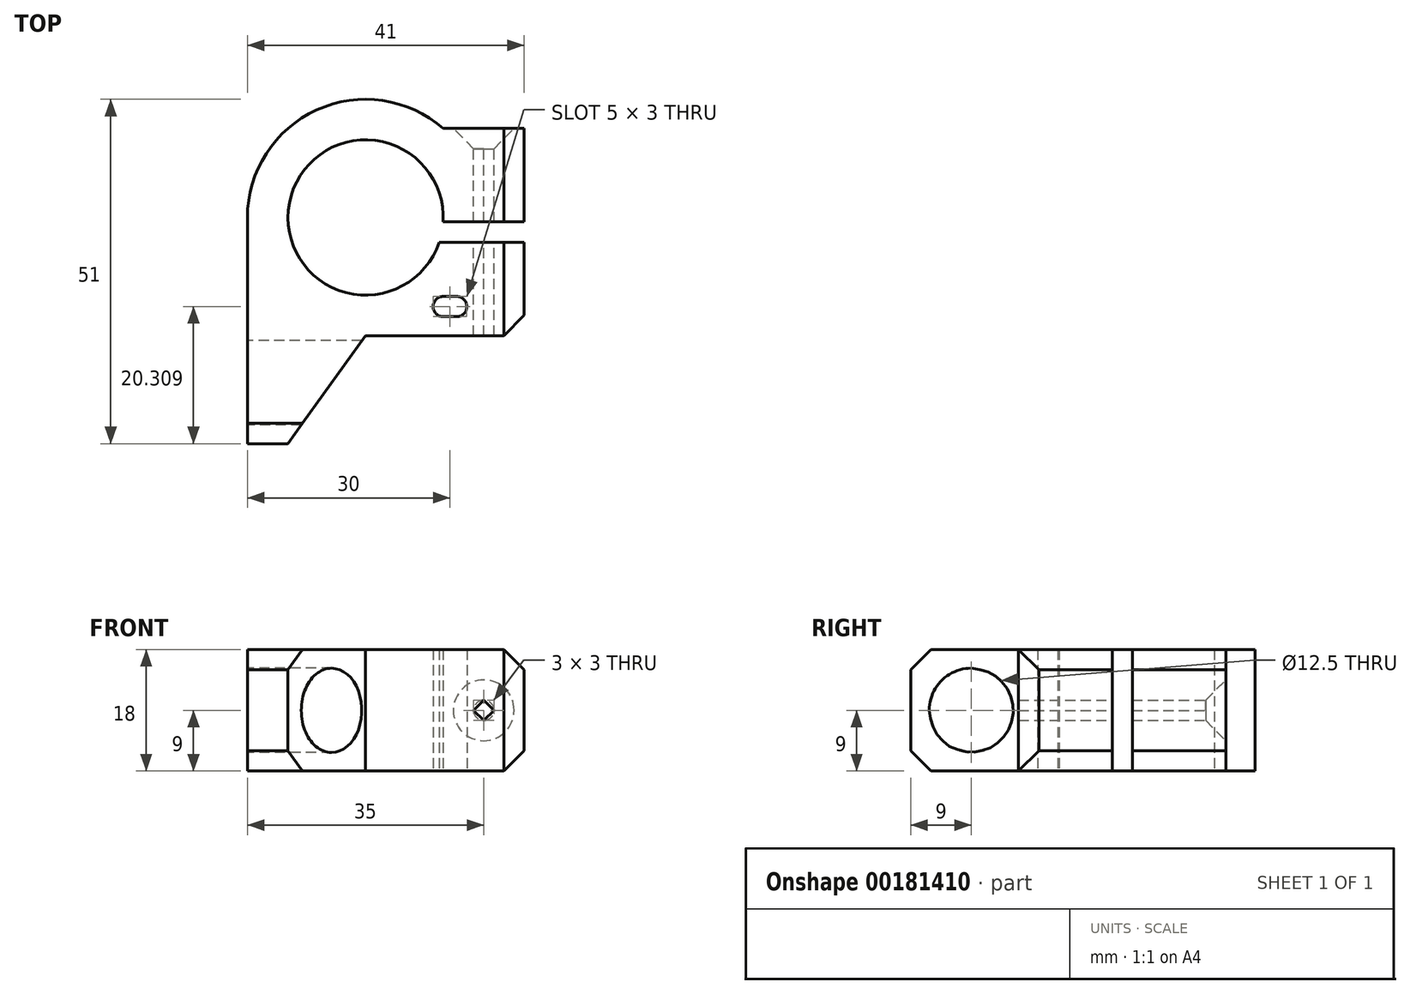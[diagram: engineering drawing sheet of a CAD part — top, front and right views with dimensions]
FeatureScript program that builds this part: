
annotation { "Feature Type Name" : "Feature", "Feature Type Description" : "" }
export const myFeature = defineFeature(function(context is Context, id is Id, definition is map)
    precondition{}
    {
        {
            var Q0;
            Q0=qCreatedBy(makeId("Top.planeOp"),FACE);
            var sketch = newSketch(context, id + "F0", { "sketchPlane" : qUnion([Q0])});
            skCircle(sketch, "E0", {"center": v(0, 0) * mm, "radius": 11.5 * mm});
            skArc(sketch, "E1", {"start": v(0, -17.5) * mm, "mid": v(6.14, -16.39) * mm, "end": v(11.5, -13.2) * mm, "construction": true});
            skLineSegment(sketch, "E2.bottom", {"start": v(-17.5, 0) * mm, "end": v(-11.5, 0) * mm, "construction": true});
            skLineSegment(sketch, "E2.top", {"start": v(-17.5, -33.5) * mm, "end": v(-11.5, -33.5) * mm});
            skLineSegment(sketch, "E2.left", {"start": v(-17.5, 0) * mm, "end": v(-17.5, -33.5) * mm});
            skLineSegment(sketch, "E3", {"start": v(0, -17.5) * mm, "end": v(-17.5, -17.5) * mm, "construction": true});
            skLineSegment(sketch, "E4", {"start": v(-11.5, -33.5) * mm, "end": v(0, -17.5) * mm});
            skLineSegment(sketch, "E5.bottom", {"start": v(11.5, 13.2) * mm, "end": v(23.5, 13.2) * mm});
            skLineSegment(sketch, "E5.top", {"start": v(11.5, -13.2) * mm, "end": v(23.5, -13.2) * mm, "construction": true});
            skLineSegment(sketch, "E5.left", {"start": v(11.5, 13.2) * mm, "end": v(11.5, 0) * mm, "construction": true});
            skLineSegment(sketch, "E5.right", {"start": v(23.5, 13.2) * mm, "end": v(23.5, -13.2) * mm});
            skPoint(sketch, "E5.middle", {"position": v(17.5, 0) * mm});
            skArc(sketch, "E6.trimOffspring", {"start": v(11.5, 13.2) * mm, "mid": v(-7.25, 15.93) * mm, "end": v(-17.5, 0) * mm});
            skLineSegment(sketch, "E7", {"start": v(0, -17.5) * mm, "end": v(23.5, -17.5) * mm});
            skLineSegment(sketch, "E8", {"start": v(23.5, -17.5) * mm, "end": v(23.5, -13.2) * mm});
            skLineSegment(sketch, "E9", {"start": v(11.5, -13.2) * mm, "end": v(13.5, -13.2) * mm});
            skArc(sketch, "E10.0.startCap", {"start": v(11.5, -14.7) * mm, "mid": v(10, -13.2) * mm, "end": v(11.5, -11.7) * mm});
            skArc(sketch, "E10.0.endCap", {"start": v(13.5, -11.7) * mm, "mid": v(15, -13.2) * mm, "end": v(13.5, -14.7) * mm});
            skLineSegment(sketch, "E10.0.left", {"start": v(11.5, -11.7) * mm, "end": v(13.5, -11.7) * mm});
            skLineSegment(sketch, "E10.0.right", {"start": v(11.5, -14.7) * mm, "end": v(13.5, -14.7) * mm});
            skSolve(sketch);
        }
        {
            var Q0;
            Q0=makeQuery(id+"F0.imprint","IMPRINT",FACE,{"disambiguationData":[TD([[makeQuery(id+"F0.imprint","IMPRINT",EDGE,{"derivedFrom":sQuery(id+"F0.wireOp",EDGE,"E0")}),-1.0]])]});
            extrude(context, id + "F1", {"entities" : qUnion([Q0]), "depth" : 18 * mm});
        }
        {
            var Q0;
            Q0=makeQuery(id+"F1.opExtrude","SWEPT_FACE",FACE,{"disambiguationData":[OSD([sQuery(id+"F0.wireOp",EDGE,"E2.left")])]});
            var sketch = newSketch(context, id + "F2", { "sketchPlane" : qUnion([Q0])});
            skCircle(sketch, "E11", {"center": v(24.5, 9) * mm, "radius": 6.25 * mm});
            skLineSegment(sketch, "E12", {"start": v(33.5, 9) * mm, "end": v(24.5, 9) * mm, "construction": true});
            skSolve(sketch);
        }
        {
            var Q0;
            Q0=makeQuery(id+"F2.imprint","IMPRINT",FACE,{"disambiguationData":[TD([[makeQuery(id+"F2.imprint","IMPRINT",EDGE,{"derivedFrom":sQuery(id+"F2.wireOp",EDGE,"E11")}),1.0]])]});
            extrude(context, id + "F3", {"entities" : qUnion([Q0]), "operationType" : NewBodyOperationType.REMOVE, "endBound" : BoundingType.THROUGH_ALL, "oppositeDirection" : true, "depth" : 25 * mm});
        }
        {
            var Q0;
            Q0=makeQuery(id+"F1.opExtrude","SWEPT_FACE",FACE,{"disambiguationData":[OSD([sQuery(id+"F0.wireOp",EDGE,"E5.bottom")])]});
            var sketch = newSketch(context, id + "F4", { "sketchPlane" : qUnion([Q0])});
            skLineSegment(sketch, "E13", {"start": v(-17.5, 18) * mm, "end": v(-17.5, 0) * mm, "construction": true});
            skLineSegment(sketch, "E14", {"start": v(-11.5, 9) * mm, "end": v(-23.5, 9) * mm, "construction": true});
            skCircle(sketch, "E15", {"center": v(-17.5, 9) * mm, "radius": 4.5 * mm});
            skLineSegment(sketch, "E16.bottom", {"start": v(-19, 7.5) * mm, "end": v(-16, 7.5) * mm, "construction": true});
            skLineSegment(sketch, "E16.top", {"start": v(-19, 10.5) * mm, "end": v(-16, 10.5) * mm, "construction": true});
            skLineSegment(sketch, "E16.left", {"start": v(-19, 7.5) * mm, "end": v(-19, 10.5) * mm, "construction": true});
            skLineSegment(sketch, "E16.right", {"start": v(-16, 7.5) * mm, "end": v(-16, 10.5) * mm, "construction": true});
            skLineSegment(sketch, "E17", {"start": v(-17.5, 10.5) * mm, "end": v(-19, 9) * mm});
            skLineSegment(sketch, "E18", {"start": v(-19, 9) * mm, "end": v(-17.5, 7.5) * mm});
            skLineSegment(sketch, "E19", {"start": v(-17.5, 7.5) * mm, "end": v(-16, 9) * mm});
            skLineSegment(sketch, "E20", {"start": v(-16, 9) * mm, "end": v(-17.5, 10.5) * mm});
            skSolve(sketch);
        }
        {
            var Q0;
            Q0 = qSketchRegion(id + "F4", true);
            extrude(context, id + "F5", {"entities" : qUnion([Q0]), "operationType" : NewBodyOperationType.REMOVE, "oppositeDirection" : true, "depth" : 3 * mm});
        }
        {
            var Q0;
            Q0=makeQuery(id+"F5.boolean.opBoolean","COPY",EDGE,{"derivedFrom":makeQuery(id+"F5.opExtrude","CAP_EDGE",EDGE,{"disambiguationData":[OSD([sQuery(id+"F4.wireOp",EDGE,"E15")])],"isStart":false})});
            chamfer(context, id + "F6", {"entities" : qUnion([Q0]), "width" : 3 * mm, "tangentPropagation" : true});
        }
        {
            var Q0;
            Q0=makeQuery(id+"F5.boolean.opBoolean","SPLIT",FACE,{"disambiguationData":[TD([makeQuery(id+"F5.opExtrude","SWEPT_FACE",FACE,{"disambiguationData":[OSD([sQuery(id+"F4.wireOp",EDGE,"E17")])]})])],"derivedFrom":makeQuery(id+"F1.opExtrude","SWEPT_FACE",FACE,{"disambiguationData":[OSD([sQuery(id+"F0.wireOp",EDGE,"E5.bottom")])]})});
            extrude(context, id + "F7", {"entities" : qUnion([Q0]), "operationType" : NewBodyOperationType.REMOVE, "endBound" : BoundingType.THROUGH_ALL, "oppositeDirection" : true, "depth" : 25 * mm});
        }
        {
            var Q0;
            Q0=makeQuery(id+"F1.opExtrude","CAP_FACE",FACE,{"disambiguationData":[OSD([sQuery(id+"F0.wireOp",EDGE,"E0"),sQuery(id+"F0.wireOp",EDGE,"E1"),sQuery(id+"F0.wireOp",EDGE,"E2.top"),sQuery(id+"F0.wireOp",EDGE,"E2.left"),sQuery(id+"F0.wireOp",EDGE,"E4"),sQuery(id+"F0.wireOp",EDGE,"E5.bottom"),sQuery(id+"F0.wireOp",EDGE,"E5.top"),sQuery(id+"F0.wireOp",EDGE,"E5.right"),sQuery(id+"F0.wireOp",EDGE,"E6.trimOffspring")])],"isStart":true});
            var sketch = newSketch(context, id + "F8", { "sketchPlane" : qUnion([Q0])});
            skLineSegment(sketch, "E21", {"start": v(23.5, 2.15) * mm, "end": v(11.3, 2.15) * mm, "construction": true});
            skLineSegment(sketch, "E22", {"start": v(23.5, 3.65) * mm, "end": v(10.9, 3.65) * mm});
            skLineSegment(sketch, "E23.MirrorCS", {"start": v(23.5, 0.65) * mm, "end": v(10.9, 0.65) * mm});
            skSolve(sketch);
        }
        {
            var Q0;
            {var subQ0=sQuery(id+"F8.wireOp",EDGE,"E22");Q0=makeQuery(id+"F8.imprint","IMPRINT",FACE,{"disambiguationData":[TD([[makeQuery(id+"F8.imprint","IMPRINT",EDGE,{"derivedFrom":subQ0}),1.0]])]});}
            extrude(context, id + "F9", {"entities" : qUnion([Q0]), "operationType" : NewBodyOperationType.REMOVE, "endBound" : BoundingType.THROUGH_ALL, "oppositeDirection" : true, "depth" : 25 * mm});
        }
        {
            var Q0;
            {var subQ0=sQuery(id+"F0.wireOp",EDGE,"E5.right");var subQ1=sQuery(id+"F0.wireOp",EDGE,"E5.top");Q0=makeQuery(id+"F9.boolean.opBoolean","SPLIT",EDGE,{"disambiguationData":[TD([makeQuery(id+"F1.opExtrude","SWEPT_FACE",FACE,{"disambiguationData":[OSD([subQ1])]})])],"derivedFrom":makeQuery(id+"F1.opExtrude","CAP_EDGE",EDGE,{"disambiguationData":[OSD([subQ0])],"isStart":true})});}
            var Q1;
            {var subQ0=sQuery(id+"F0.wireOp",EDGE,"E5.right");var subQ1=sQuery(id+"F0.wireOp",EDGE,"E5.bottom");Q1=makeQuery(id+"F9.boolean.opBoolean","SPLIT",EDGE,{"disambiguationData":[TD([makeQuery(id+"F1.opExtrude","SWEPT_FACE",FACE,{"disambiguationData":[OSD([subQ1])]})])],"derivedFrom":makeQuery(id+"F1.opExtrude","CAP_EDGE",EDGE,{"disambiguationData":[OSD([subQ0])],"isStart":true})});}
            var Q2;
            {var subQ0=sQuery(id+"F0.wireOp",EDGE,"E5.right");var subQ1=sQuery(id+"F0.wireOp",EDGE,"E5.bottom");Q2=makeQuery(id+"F9.boolean.opBoolean","SPLIT",EDGE,{"disambiguationData":[TD([makeQuery(id+"F1.opExtrude","SWEPT_FACE",FACE,{"disambiguationData":[OSD([subQ1])]})])],"derivedFrom":makeQuery(id+"F1.opExtrude","CAP_EDGE",EDGE,{"disambiguationData":[OSD([subQ0])],"isStart":false})});}
            var Q3;
            {var subQ0=sQuery(id+"F0.wireOp",EDGE,"E5.right");var subQ1=sQuery(id+"F0.wireOp",EDGE,"E5.top");Q3=makeQuery(id+"F9.boolean.opBoolean","SPLIT",EDGE,{"disambiguationData":[TD([makeQuery(id+"F1.opExtrude","SWEPT_FACE",FACE,{"disambiguationData":[OSD([subQ1])]})])],"derivedFrom":makeQuery(id+"F1.opExtrude","CAP_EDGE",EDGE,{"disambiguationData":[OSD([subQ0])],"isStart":false})});}
            var Q4;
            {var subQ0=sQuery(id+"F0.wireOp",EDGE,"E8");var subQ1=sQuery(id+"F0.wireOp",EDGE,"E7");var subQ2=sQuery(id+"F0.wireOp",EDGE,"E5.right");Q4=makeQuery(id+"F9.boolean.opBoolean","SPLIT",EDGE,{"disambiguationData":[TD([makeQuery(id+"F1.opExtrude","SWEPT_FACE",FACE,{"disambiguationData":[OSD([subQ1])]})])],"derivedFrom":makeQuery(id+"F1.opExtrude","CAP_EDGE",EDGE,{"disambiguationData":[OSD([subQ2,subQ0])],"isStart":true})});}
            var Q5;
            {var subQ0=sQuery(id+"F0.wireOp",EDGE,"E8");var subQ1=sQuery(id+"F0.wireOp",EDGE,"E7");var subQ2=sQuery(id+"F0.wireOp",EDGE,"E5.right");Q5=makeQuery(id+"F9.boolean.opBoolean","SPLIT",EDGE,{"disambiguationData":[TD([makeQuery(id+"F1.opExtrude","SWEPT_FACE",FACE,{"disambiguationData":[OSD([subQ1])]})])],"derivedFrom":makeQuery(id+"F1.opExtrude","CAP_EDGE",EDGE,{"disambiguationData":[OSD([subQ2,subQ0])],"isStart":false})});}
            var Q6;
            Q6=makeQuery(id+"F1.opExtrude","SWEPT_EDGE",EDGE,{"disambiguationData":[OSD([sQuery(id+"F0.wireOp",EDGE,"E7"),sQuery(id+"F0.wireOp",EDGE,"E8")])]});
            chamfer(context, id + "F10", {"entities" : qUnion([Q0, Q1, Q2, Q3, Q4, Q5, Q6]), "width" : 3 * mm, "tangentPropagation" : true});
        }
        {
            var Q0;
            Q0=makeQuery(id+"F1.opExtrude","CAP_EDGE",EDGE,{"disambiguationData":[OSD([sQuery(id+"F0.wireOp",EDGE,"E2.top")])],"isStart":false});
            var Q1;
            Q1=makeQuery(id+"F1.opExtrude","CAP_EDGE",EDGE,{"disambiguationData":[OSD([sQuery(id+"F0.wireOp",EDGE,"E2.top")])],"isStart":true});
            chamfer(context, id + "F11", {"entities" : qUnion([Q0, Q1]), "width" : 3 * mm, "tangentPropagation" : true});
        }
    });
